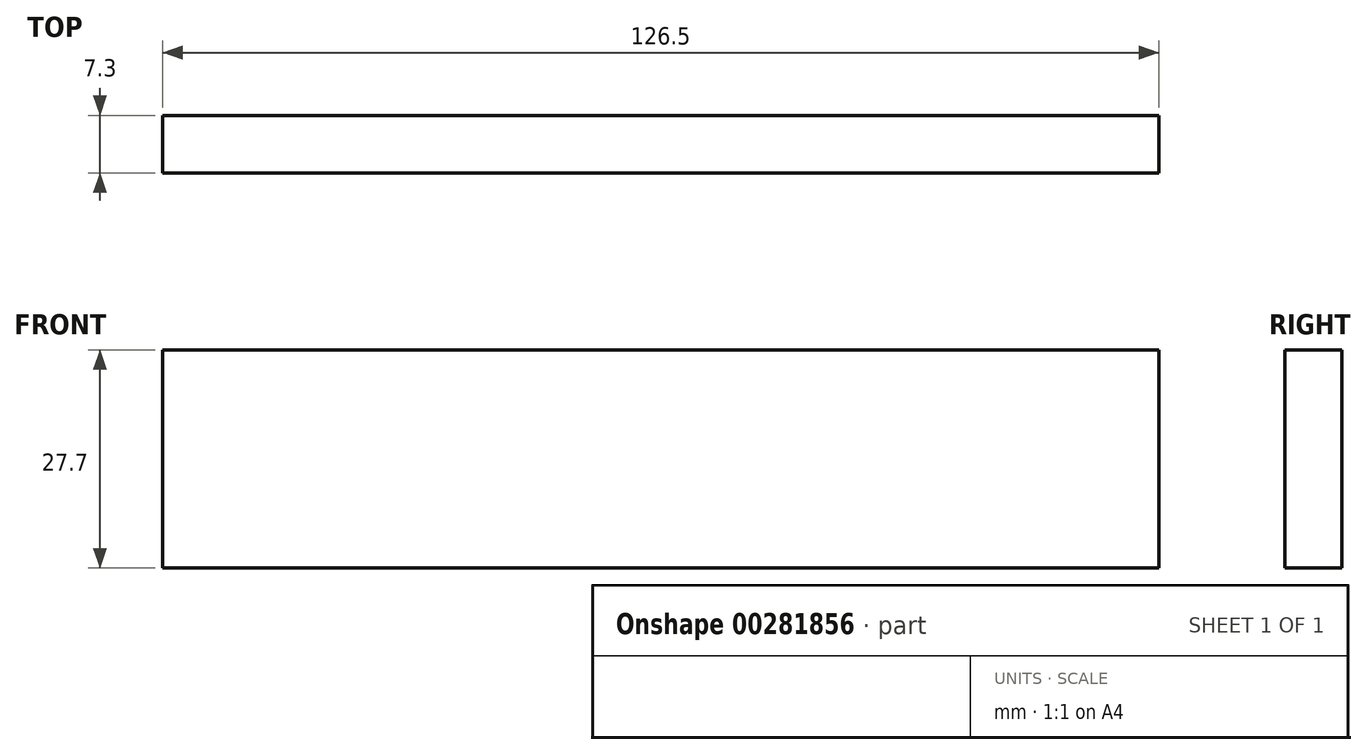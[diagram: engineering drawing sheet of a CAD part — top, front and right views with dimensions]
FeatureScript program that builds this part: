
annotation { "Feature Type Name" : "Feature", "Feature Type Description" : "" }
export const myFeature = defineFeature(function(context is Context, id is Id, definition is map)
    precondition{}
    {
        {
            var Q0;
            Q0=qCreatedBy(makeId("Front.planeOp"),FACE);
            var sketch = newSketch(context, id + "F0", { "sketchPlane" : qUnion([Q0])});
            skLineSegment(sketch, "E0.bottom", {"start": v(63.25, -13.85) * mm, "end": v(-63.25, -13.85) * mm});
            skLineSegment(sketch, "E0.top", {"start": v(63.25, 13.85) * mm, "end": v(-63.25, 13.85) * mm});
            skLineSegment(sketch, "E0.left", {"start": v(63.25, -13.85) * mm, "end": v(63.25, 13.85) * mm});
            skLineSegment(sketch, "E0.right", {"start": v(-63.25, -13.85) * mm, "end": v(-63.25, 13.85) * mm});
            skPoint(sketch, "E0.middle", {"position": v(0, 0) * mm});
            skSolve(sketch);
        }
        {
            var Q0;
            Q0=makeQuery(id+"F0.imprint","IMPRINT",FACE,{"disambiguationData":[TD([[makeQuery(id+"F0.imprint","IMPRINT",EDGE,{"derivedFrom":sQuery(id+"F0.wireOp",EDGE,"E0.bottom")}),-1.0]])]});
            extrude(context, id + "F1", {"entities" : qUnion([Q0]), "endBound" : BoundingType.SYMMETRIC, "depth" : 7.3 * mm});
        }
    });
